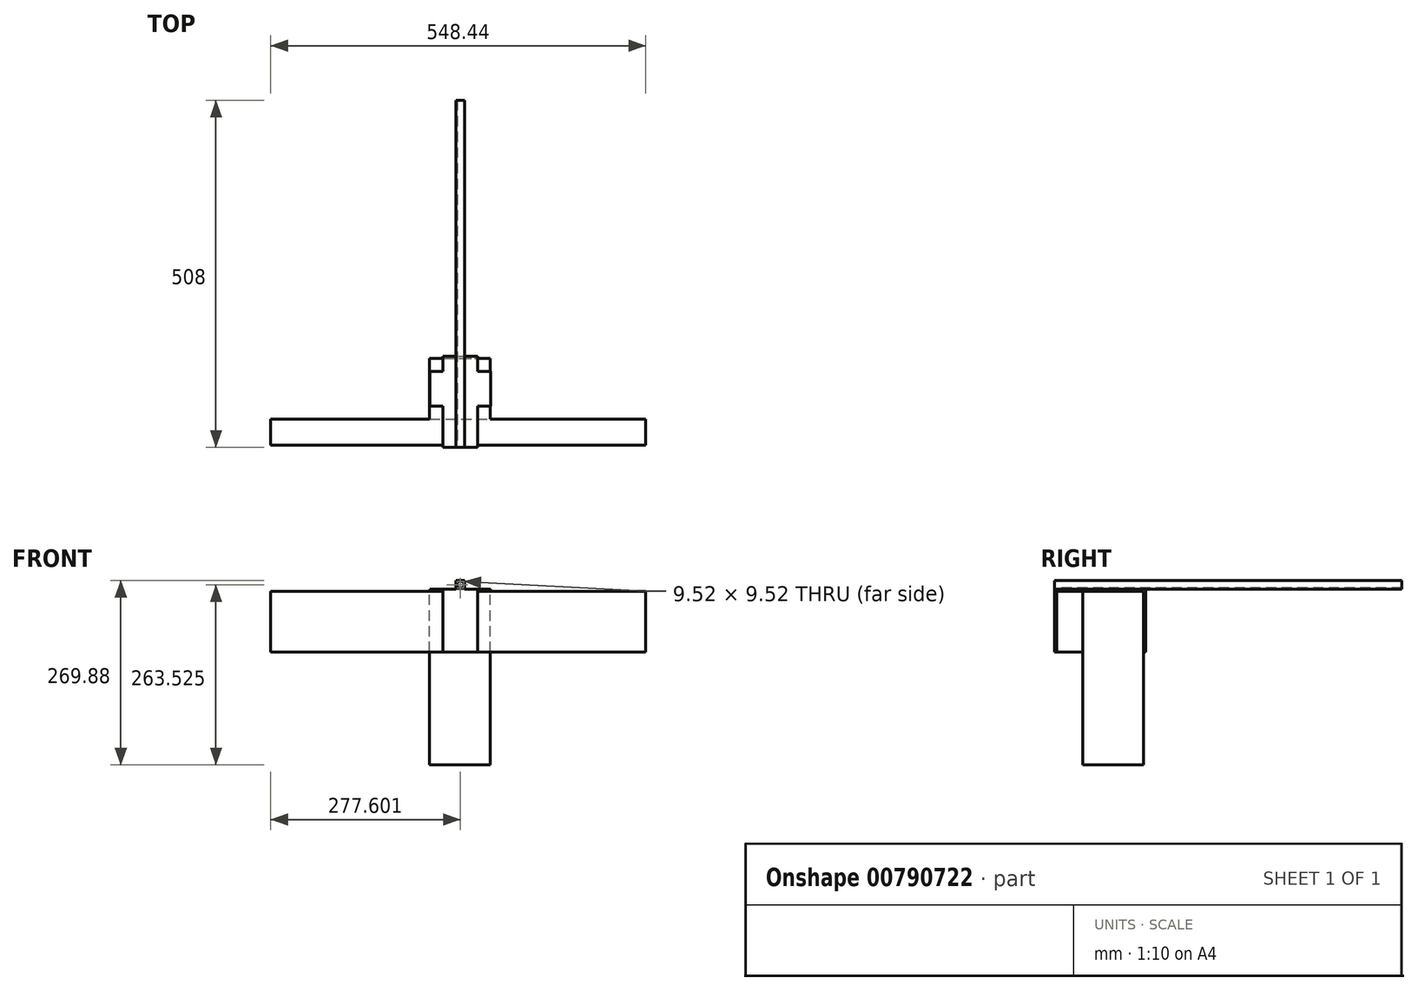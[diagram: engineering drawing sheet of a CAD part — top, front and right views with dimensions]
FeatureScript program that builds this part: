
annotation { "Feature Type Name" : "Feature", "Feature Type Description" : "" }
export const myFeature = defineFeature(function(context is Context, id is Id, definition is map)
    precondition{}
    {
        {
            var Q0;
            Q0=qCreatedBy(makeId("Top.planeOp"),FACE);
            var sketch = newSketch(context, id + "F0", { "sketchPlane" : qUnion([Q0])});
            skLineSegment(sketch, "E0.bottom", {"start": v(-41.37, 127) * mm, "end": v(47.53, 127) * mm});
            skLineSegment(sketch, "E0.top", {"start": v(-41.37, 38.1) * mm, "end": v(47.53, 38.1) * mm});
            skLineSegment(sketch, "E0.left", {"start": v(-41.37, 127) * mm, "end": v(-41.37, 38.1) * mm});
            skLineSegment(sketch, "E0.right", {"start": v(47.53, 127) * mm, "end": v(47.53, 38.1) * mm});
            skLineSegment(sketch, "E1.bottom", {"start": v(-273.88, 38.1) * mm, "end": v(274.56, 38.1) * mm});
            skLineSegment(sketch, "E1.top", {"start": v(-273.88, 0) * mm, "end": v(274.56, 0) * mm});
            skLineSegment(sketch, "E1.left", {"start": v(-273.88, 38.1) * mm, "end": v(-273.88, 0) * mm});
            skLineSegment(sketch, "E1.right", {"start": v(274.56, 38.1) * mm, "end": v(274.56, 0) * mm});
            skSolve(sketch);
        }
        {
            var Q0;
            Q0=makeQuery(id+"F0.imprint","IMPRINT",FACE,{"disambiguationData":[TD([[makeQuery(id+"F0.imprint","IMPRINT",EDGE,{"derivedFrom":sQuery(id+"F0.wireOp",EDGE,"E0.bottom")}),-1.0]])]});
            extrude(context, id + "F1", {"entities" : qUnion([Q0]), "depth" : -254 * mm, "offsetDistance" : 25.4 * mm});
        }
        {
            var Q0;
            Q0=makeQuery(id+"F0.imprint","IMPRINT",FACE,{"disambiguationData":[TD([[makeQuery(id+"F0.imprint","IMPRINT",EDGE,{"derivedFrom":sQuery(id+"F0.wireOp",EDGE,"E1.top")}),1.0]])]});
            extrude(context, id + "F2", {"entities" : qUnion([Q0]), "operationType" : NewBodyOperationType.ADD, "depth" : -88.9 * mm, "offsetDistance" : 25.4 * mm});
        }
        {
            var Q0;
            Q0=qCreatedBy(makeId("Top.planeOp"),FACE);
            var sketch = newSketch(context, id + "F3", { "sketchPlane" : qUnion([Q0])});
            skLineSegment(sketch, "E2.bottom", {"start": v(-21.68, 130.17) * mm, "end": v(29.12, 130.17) * mm});
            skLineSegment(sketch, "E2.top", {"start": v(-21.68, -3.18) * mm, "end": v(29.12, -3.18) * mm});
            skLineSegment(sketch, "E2.left", {"start": v(-21.68, 130.17) * mm, "end": v(-21.68, -3.18) * mm});
            skLineSegment(sketch, "E2.right", {"start": v(29.12, 130.17) * mm, "end": v(29.12, -3.18) * mm});
            skSolve(sketch);
        }
        {
            var Q0;
            Q0 = qSketchRegion(id + "F3", true);
            extrude(context, id + "F4", {"entities" : qUnion([Q0]), "operationType" : NewBodyOperationType.ADD, "depth" : 3.17 * mm, "offsetDistance" : 25.4 * mm});
        }
        {
            var Q0;
            {var subQ0=sQuery(id+"F3.wireOp",EDGE,"E2.top");var subQ2=sQuery(id+"F0.wireOp",EDGE,"E1.top");var subQ3=sQuery(id+"F3.wireOp",EDGE,"E2.left");var subQ4=sQuery(id+"F3.wireOp",EDGE,"E2.right");Q0=makeQuery(id+"F4.boolean.opBoolean","SPLIT",FACE,{"disambiguationData":[TD([makeQuery(id+"F2.opExtrude","SWEPT_FACE",FACE,{"disambiguationData":[OSD([subQ2])]})])],"derivedFrom":makeQuery(id+"F4.opExtrude","CAP_FACE",FACE,{"disambiguationData":[OSD([sQuery(id+"F3.wireOp",EDGE,"E2.bottom"),subQ0,subQ3,subQ4])],"isStart":true})});}
            var sketch = newSketch(context, id + "F5", { "sketchPlane" : qUnion([Q0])});
            skLineSegment(sketch, "E3.bottom", {"start": v(-21.68, 3.18) * mm, "end": v(29.12, 3.18) * mm});
            skLineSegment(sketch, "E3.top", {"start": v(-21.68, 0) * mm, "end": v(29.12, 0) * mm});
            skLineSegment(sketch, "E3.left", {"start": v(-21.68, 3.18) * mm, "end": v(-21.68, 0) * mm});
            skLineSegment(sketch, "E3.right", {"start": v(29.12, 3.18) * mm, "end": v(29.12, 0) * mm});
            skSolve(sketch);
        }
        {
            var Q0;
            Q0=makeQuery(id+"F5.imprint","IMPRINT",FACE,{"disambiguationData":[TD([[makeQuery(id+"F5.imprint","IMPRINT",EDGE,{"derivedFrom":sQuery(id+"F5.wireOp",EDGE,"E3.bottom")}),-1.0]])]});
            var sketch = newSketch(context, id + "F6", { "sketchPlane" : qUnion([Q0])});
            skLineSegment(sketch, "E4.bottom", {"start": v(-21.62, 3.17) * mm, "end": v(29.1, 3.17) * mm});
            skLineSegment(sketch, "E4.top", {"start": v(-21.62, 0) * mm, "end": v(29.1, 0) * mm});
            skLineSegment(sketch, "E4.left", {"start": v(-21.62, 3.17) * mm, "end": v(-21.62, 0) * mm});
            skLineSegment(sketch, "E4.right", {"start": v(29.1, 3.17) * mm, "end": v(29.1, 0) * mm});
            skSolve(sketch);
        }
        {
            var Q0;
            Q0 = qSketchRegion(id + "F6", true);
            extrude(context, id + "F7", {"entities" : qUnion([Q0]), "operationType" : NewBodyOperationType.ADD, "depth" : 88.9 * mm, "offsetDistance" : 25.4 * mm});
        }
        {
            var Q0;
            Q0=makeQuery(id+"F4.opExtrude","CAP_FACE",FACE,{"disambiguationData":[OSD([sQuery(id+"F3.wireOp",EDGE,"E2.bottom"),sQuery(id+"F3.wireOp",EDGE,"E2.top"),sQuery(id+"F3.wireOp",EDGE,"E2.left"),sQuery(id+"F3.wireOp",EDGE,"E2.right")])],"isStart":false});
            var sketch = newSketch(context, id + "F8", { "sketchPlane" : qUnion([Q0])});
            skLineSegment(sketch, "E5.bottom", {"start": v(-2.63, 504.82) * mm, "end": v(10.07, 504.82) * mm});
            skLineSegment(sketch, "E5.top", {"start": v(-2.63, -3.18) * mm, "end": v(10.07, -3.18) * mm});
            skLineSegment(sketch, "E5.left", {"start": v(-2.63, 504.82) * mm, "end": v(-2.63, -3.18) * mm});
            skLineSegment(sketch, "E5.right", {"start": v(10.07, 504.82) * mm, "end": v(10.07, -3.18) * mm});
            skSolve(sketch);
        }
        {
            var Q0;
            {var subQ0=sQuery(id+"F8.wireOp",EDGE,"E5.top");Q0=makeQuery(id+"F8.imprint","IMPRINT",FACE,{"disambiguationData":[TD([[makeQuery(id+"F8.imprint","IMPRINT",EDGE,{"derivedFrom":subQ0}),1.0]])]});}
            var Q1;
            {var subQ0=sQuery(id+"F8.wireOp",EDGE,"E5.bottom");Q1=makeQuery(id+"F8.imprint","IMPRINT",FACE,{"disambiguationData":[TD([[makeQuery(id+"F8.imprint","IMPRINT",EDGE,{"derivedFrom":subQ0}),-1.0]])]});}
            extrude(context, id + "F9", {"entities" : qUnion([Q0, Q1]), "operationType" : NewBodyOperationType.ADD, "depth" : 12.7 * mm, "offsetDistance" : 25.4 * mm});
        }
        {
            var Q0;
            Q0=makeQuery(id+"F9.boolean.opBoolean","MERGE",FACE,{"derivedFrom":[makeQuery(id+"F4.opExtrude","SWEPT_FACE",FACE,{"disambiguationData":[OSD([sQuery(id+"F3.wireOp",EDGE,"E2.top")])]}),makeQuery(id+"F9.opExtrude","SWEPT_FACE",FACE,{"disambiguationData":[OSD([sQuery(id+"F8.wireOp",EDGE,"E5.top")])]})]});
            var sketch = newSketch(context, id + "F10", { "sketchPlane" : qUnion([Q0])});
            skLineSegment(sketch, "E6.bottom", {"start": v(-1.04, 14.29) * mm, "end": v(8.48, 14.29) * mm});
            skLineSegment(sketch, "E6.top", {"start": v(-1.04, 4.76) * mm, "end": v(8.48, 4.76) * mm});
            skLineSegment(sketch, "E6.left", {"start": v(-1.04, 14.29) * mm, "end": v(-1.04, 4.76) * mm});
            skLineSegment(sketch, "E6.right", {"start": v(8.48, 14.29) * mm, "end": v(8.48, 4.76) * mm});
            skSolve(sketch);
        }
        {
            var Q0;
            Q0=makeQuery(id+"F10.imprint","IMPRINT",FACE,{"disambiguationData":[TD([[makeQuery(id+"F10.imprint","IMPRINT",EDGE,{"derivedFrom":sQuery(id+"F10.wireOp",EDGE,"E6.bottom")}),-1.0]])]});
            extrude(context, id + "F11", {"entities" : qUnion([Q0]), "operationType" : NewBodyOperationType.REMOVE, "oppositeDirection" : true, "depth" : 558.8 * mm, "offsetDistance" : 25.4 * mm});
        }
        {
            var Q0;
            {var subQ1=sQuery(id+"F0.wireOp",EDGE,"E0.bottom");var subQ2=sQuery(id+"F3.wireOp",EDGE,"E2.bottom");var subQ3=sQuery(id+"F3.wireOp",EDGE,"E2.left");var subQ4=sQuery(id+"F3.wireOp",EDGE,"E2.right");Q0=makeQuery(id+"F4.boolean.opBoolean","SPLIT",FACE,{"disambiguationData":[TD([makeQuery(id+"F1.opExtrude","SWEPT_FACE",FACE,{"disambiguationData":[OSD([subQ1])]})])],"derivedFrom":makeQuery(id+"F4.opExtrude","CAP_FACE",FACE,{"disambiguationData":[OSD([subQ2,sQuery(id+"F3.wireOp",EDGE,"E2.top"),subQ3,subQ4])],"isStart":true})});}
            var sketch = newSketch(context, id + "F12", { "sketchPlane" : qUnion([Q0])});
            skLineSegment(sketch, "E7.bottom", {"start": v(29.12, -130.17) * mm, "end": v(-21.68, -130.17) * mm});
            skLineSegment(sketch, "E7.top", {"start": v(29.12, -127) * mm, "end": v(-21.68, -127) * mm});
            skLineSegment(sketch, "E7.left", {"start": v(29.12, -130.17) * mm, "end": v(29.12, -127) * mm});
            skLineSegment(sketch, "E7.right", {"start": v(-21.68, -130.17) * mm, "end": v(-21.68, -127) * mm});
            skSolve(sketch);
        }
        {
            var Q0;
            Q0 = qSketchRegion(id + "F12", true);
            extrude(context, id + "F13", {"entities" : qUnion([Q0]), "operationType" : NewBodyOperationType.ADD, "depth" : 88.9 * mm, "offsetDistance" : 25.4 * mm});
        }
        {
            var Q0;
            Q0=makeQuery(id+"F13.boolean.opBoolean","MERGE",FACE,{"derivedFrom":[makeQuery(id+"F4.opExtrude","SWEPT_FACE",FACE,{"disambiguationData":[OSD([sQuery(id+"F3.wireOp",EDGE,"E2.left")])]}),makeQuery(id+"F13.opExtrude","SWEPT_FACE",FACE,{"disambiguationData":[OSD([sQuery(id+"F12.wireOp",EDGE,"E7.right")])]})]});
            var sketch = newSketch(context, id + "F14", { "sketchPlane" : qUnion([Q0])});
            skLineSegment(sketch, "E8.bottom", {"start": v(-107.95, 3.18) * mm, "end": v(-57.15, 3.18) * mm});
            skLineSegment(sketch, "E8.top", {"start": v(-107.95, 0) * mm, "end": v(-57.15, 0) * mm});
            skLineSegment(sketch, "E8.left", {"start": v(-107.95, 3.18) * mm, "end": v(-107.95, 0) * mm});
            skLineSegment(sketch, "E8.right", {"start": v(-57.15, 3.18) * mm, "end": v(-57.15, 0) * mm});
            skSolve(sketch);
        }
        {
            var Q0;
            Q0=makeQuery(id+"F14.imprint","IMPRINT",FACE,{"disambiguationData":[TD([[makeQuery(id+"F14.imprint","IMPRINT",EDGE,{"derivedFrom":sQuery(id+"F14.wireOp",EDGE,"E8.bottom")}),-1.0]])]});
            extrude(context, id + "F15", {"entities" : qUnion([Q0]), "operationType" : NewBodyOperationType.ADD, "depth" : 19.05 * mm, "offsetDistance" : 25.4 * mm});
        }
        {
            var Q0;
            Q0=makeQuery(id+"F13.boolean.opBoolean","MERGE",FACE,{"derivedFrom":[makeQuery(id+"F4.opExtrude","SWEPT_FACE",FACE,{"disambiguationData":[OSD([sQuery(id+"F3.wireOp",EDGE,"E2.right")])]}),makeQuery(id+"F13.opExtrude","SWEPT_FACE",FACE,{"disambiguationData":[OSD([sQuery(id+"F12.wireOp",EDGE,"E7.left")])]})]});
            var sketch = newSketch(context, id + "F16", { "sketchPlane" : qUnion([Q0])});
            skLineSegment(sketch, "E9.bottom", {"start": v(57.15, 0) * mm, "end": v(107.95, 0) * mm});
            skLineSegment(sketch, "E9.top", {"start": v(57.15, 3.18) * mm, "end": v(107.95, 3.18) * mm});
            skLineSegment(sketch, "E9.left", {"start": v(57.15, 0) * mm, "end": v(57.15, 3.18) * mm});
            skLineSegment(sketch, "E9.right", {"start": v(107.95, 0) * mm, "end": v(107.95, 3.18) * mm});
            skSolve(sketch);
        }
        {
            var Q0;
            Q0=makeQuery(id+"F16.imprint","IMPRINT",FACE,{"disambiguationData":[TD([[makeQuery(id+"F16.imprint","IMPRINT",EDGE,{"derivedFrom":sQuery(id+"F16.wireOp",EDGE,"E9.bottom")}),-1.0]])]});
            extrude(context, id + "F17", {"entities" : qUnion([Q0]), "operationType" : NewBodyOperationType.ADD, "depth" : 19.05 * mm, "offsetDistance" : 25.4 * mm});
        }
    });
